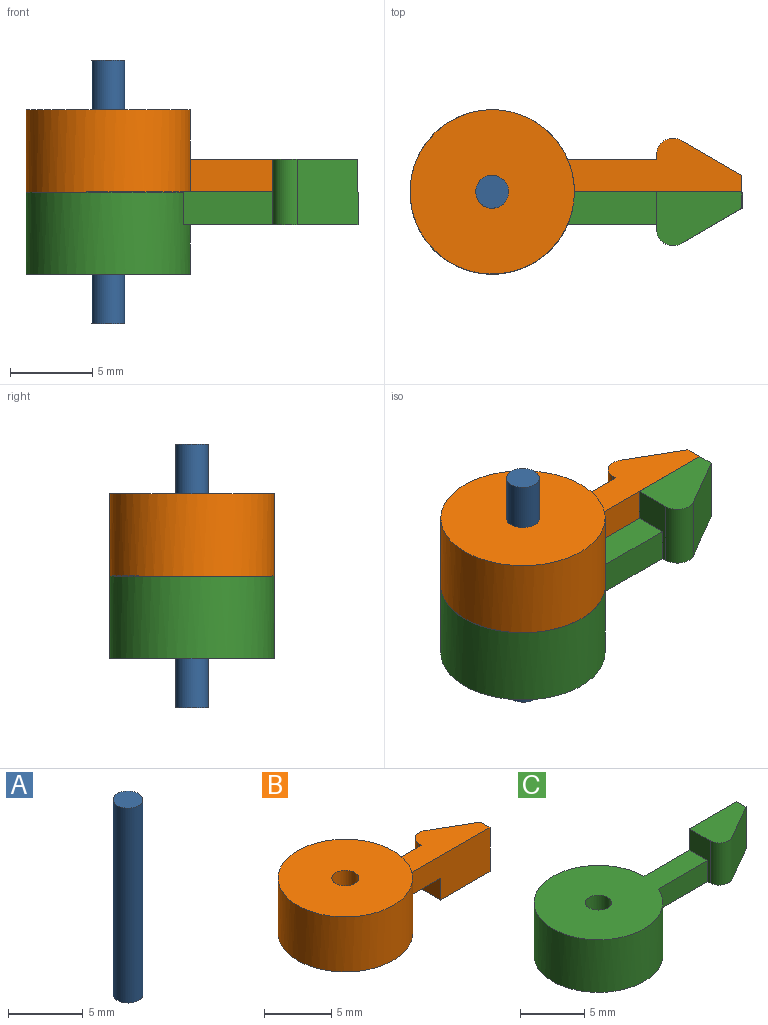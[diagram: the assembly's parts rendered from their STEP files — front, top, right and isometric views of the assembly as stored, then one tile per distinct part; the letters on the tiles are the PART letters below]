
ASSEMBLY  parts=3 mates=2
PART A: 3 faces, bbox 2x2x16 mm
  f0: cylinder r=1mm len=16mm, axis (0,0,-1), area 100.5mm2, adj f1,f2
  f1: plane 2x2mm, normal (0,0,1), area 3.1mm2, adj f0
  f2: plane 2x2mm, normal (0,0,-1), area 3.1mm2, adj f0
PART B: 12 faces, bbox 20.2x10x7 mm
  f0: cylinder r=5mm len=10mm, axis (0,0,-1), area 153mm2, adj f1,f2,f3,f4,f5
  f1: plane 10x10mm, normal (0,0,1), area 75.4mm2, adj f0,f11
  f2: plane 15x10mm, normal (0,0,-1), area 85.7mm2, adj f0,f3,f4,f8,f11
  f3: plane 10.2x4mm, normal (0,-1,0), area 30.8mm2, adj f0,f2,f5,f6,f8,f9
  f4: plane 5.42x2mm, normal (0,1,0), area 10.8mm2, adj f0,f2,f5,f8
  f5: plane 10.61x3.27mm, normal (0,0,1), area 22.6mm2, adj f0,f3,f4,f6,f7,f8,f10
  f6: plane 4x1mm, normal (1,0,0), area 4mm2, adj f3,f5,f7,f9
  f7: plane 4x3.7mm, normal (0.5,0.87,0), area 17.1mm2, adj f5,f6,f9,f10
  f8: plane 4x2.27mm, normal (-1,0,0), area 5.1mm2, adj f2,f3,f4,f5,f9,f10
  f9: plane 5.2x3.27mm, normal (0,0,-1), area 12.3mm2, adj f3,f6,f7,f8,f10
  f10: cylinder r=1mm len=4mm, axis (0,0,-1), area 8.4mm2, adj f5,f7,f8,f9
  f11: cylinder r=1mm len=5mm, axis (0,0,-1), area 31.4mm2, adj f1,f2
PART C: 12 faces, bbox 20.2x10x7 mm
  f0: cylinder r=5mm len=10mm, axis (0,0,1), area 153mm2, adj f1,f2,f3,f4,f5
  f1: plane 10x10mm, normal (0,0,-1), area 75.4mm2, adj f0,f11
  f2: plane 15x10mm, normal (0,0,1), area 85.7mm2, adj f0,f3,f4,f6,f11
  f3: plane 10.2x4mm, normal (0,1,0), area 30.8mm2, adj f0,f2,f5,f6,f8,f9
  f4: plane 5.42x2mm, normal (0,-1,0), area 10.8mm2, adj f0,f2,f5,f6
  f5: plane 10.61x3.27mm, normal (0,0,-1), area 22.6mm2, adj f0,f3,f4,f6,f7,f8,f10
  f6: plane 4x2.27mm, normal (-1,0,0), area 5.1mm2, adj f2,f3,f4,f5,f9,f10
  f7: plane 4x3.7mm, normal (0.5,-0.87,0), area 17.1mm2, adj f5,f8,f9,f10
  f8: plane 4x1mm, normal (1,0,0), area 4mm2, adj f3,f5,f7,f9
  f9: plane 5.2x3.27mm, normal (0,0,1), area 12.3mm2, adj f3,f6,f7,f8,f10
  f10: cylinder r=1mm len=4mm, axis (0,0,-1), area 8.4mm2, adj f5,f6,f7,f9
  f11: cylinder r=1mm len=5mm, axis (0,0,1), area 31.4mm2, adj f1,f2
PLACE A t=(-3.29,3.73,7.86)mm fixed
PLACE B t=(-3.29,3.73,15.86)mm
PLACE C t=(-3.29,3.73,15.86)mm
MATE revolute B.f0 <-> C.f0  axis (0,0,-1) through (-3.29,3.73,15.86)mm
MATE revolute C.f0 <-> A.f0  axis (0,0,1) through (-3.29,3.73,15.86)mm
